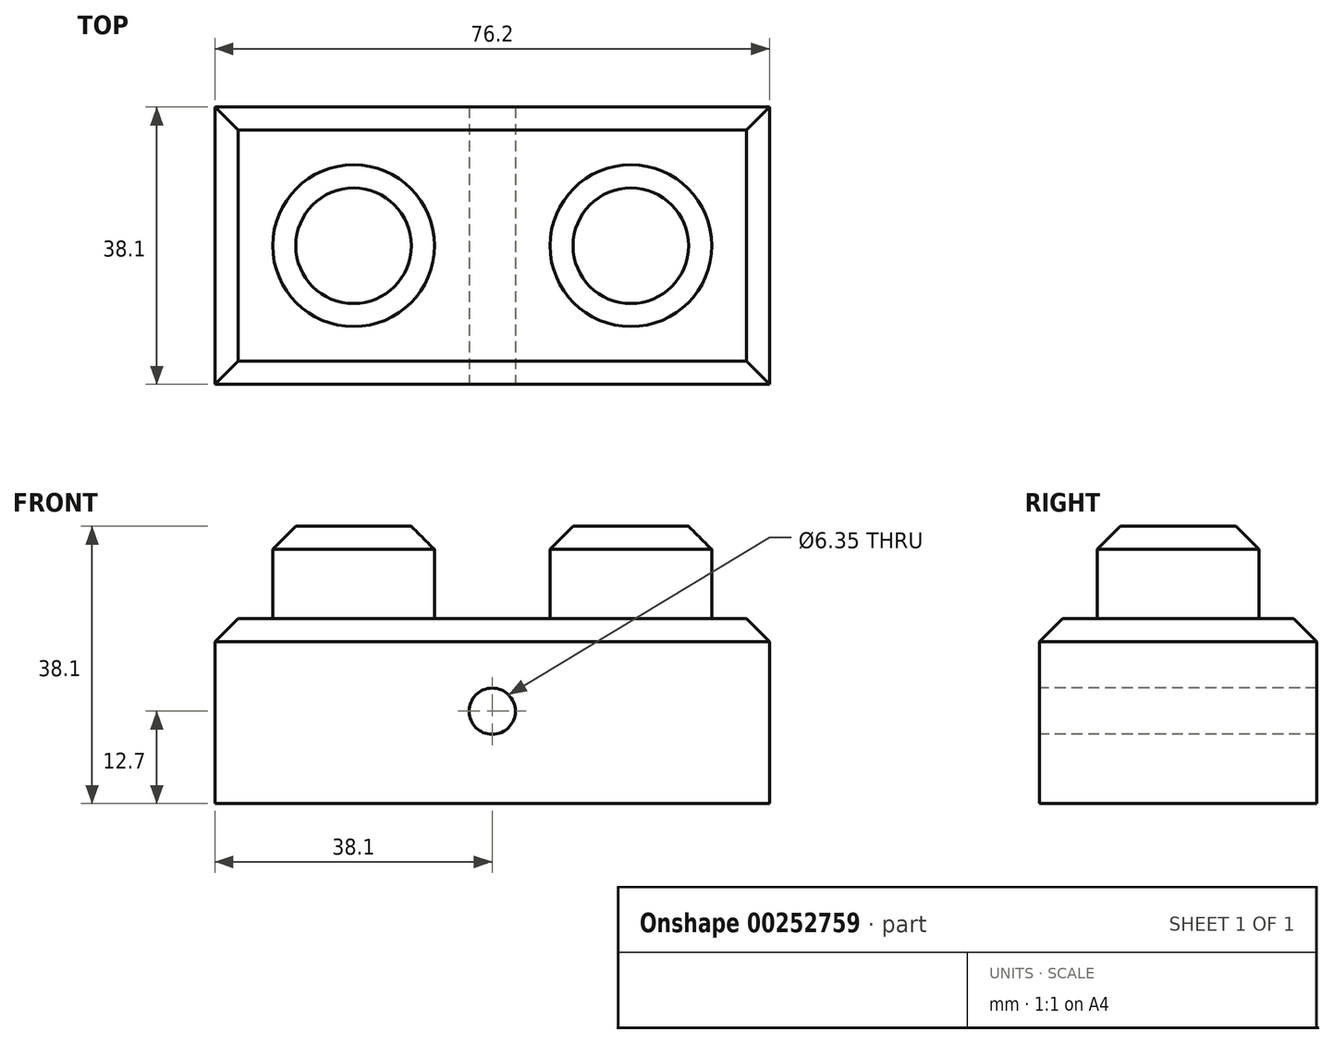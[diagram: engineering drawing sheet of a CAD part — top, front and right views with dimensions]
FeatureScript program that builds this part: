
annotation { "Feature Type Name" : "Feature", "Feature Type Description" : "" }
export const myFeature = defineFeature(function(context is Context, id is Id, definition is map)
    precondition{}
    {
        {
            var Q0;
            Q0=qCreatedBy(makeId("Top.planeOp"),FACE);
            var sketch = newSketch(context, id + "F0", { "sketchPlane" : qUnion([Q0])});
            skLineSegment(sketch, "E0.bottom", {"start": v(0, 0) * mm, "end": v(76.2, 0) * mm});
            skLineSegment(sketch, "E0.top", {"start": v(0, -38.1) * mm, "end": v(76.2, -38.1) * mm});
            skLineSegment(sketch, "E0.left", {"start": v(0, 0) * mm, "end": v(0, -38.1) * mm});
            skLineSegment(sketch, "E0.right", {"start": v(76.2, 0) * mm, "end": v(76.2, -38.1) * mm});
            skSolve(sketch);
        }
        {
            var Q0;
            Q0 = qSketchRegion(id + "F0", true);
            extrude(context, id + "F1", {"entities" : qUnion([Q0]), "depth" : 25.4 * mm});
        }
        {
            var Q0;
            Q0=makeQuery(id+"F1.opExtrude","CAP_FACE",FACE,{"disambiguationData":[OSD([sQuery(id+"F0.wireOp",EDGE,"E0.bottom"),sQuery(id+"F0.wireOp",EDGE,"E0.top"),sQuery(id+"F0.wireOp",EDGE,"E0.left"),sQuery(id+"F0.wireOp",EDGE,"E0.right")])],"isStart":false});
            var sketch = newSketch(context, id + "F2", { "sketchPlane" : qUnion([Q0])});
            skCircle(sketch, "E1", {"center": v(19.05, -19.05) * mm, "radius": 11.11 * mm});
            skCircle(sketch, "E2", {"center": v(57.15, -19.05) * mm, "radius": 11.11 * mm});
            skSolve(sketch);
        }
        {
            var Q0;
            Q0 = qSketchRegion(id + "F2", true);
            extrude(context, id + "F3", {"entities" : qUnion([Q0]), "operationType" : NewBodyOperationType.ADD, "depth" : 12.7 * mm});
        }
        {
            var Q0;
            Q0=makeQuery(id+"F1.opExtrude","SWEPT_FACE",FACE,{"disambiguationData":[OSD([sQuery(id+"F0.wireOp",EDGE,"E0.top")])]});
            var sketch = newSketch(context, id + "F4", { "sketchPlane" : qUnion([Q0])});
            skCircle(sketch, "E3", {"center": v(38.1, 12.7) * mm, "radius": 3.18 * mm});
            skSolve(sketch);
        }
        {
            var Q0;
            Q0 = qSketchRegion(id + "F4", true);
            extrude(context, id + "F5", {"entities" : qUnion([Q0]), "operationType" : NewBodyOperationType.REMOVE, "endBound" : BoundingType.THROUGH_ALL, "oppositeDirection" : true, "depth" : 25.4 * mm, "hasSecondDirection" : true, "secondDirectionBound" : SecondDirectionBoundingType.THROUGH_ALL, "secondDirectionOppositeDirection" : false, "secondDirectionDepth" : 25.4 * mm});
        }
        {
            var Q0;
            Q0=makeQuery(id+"F3.opExtrude","CAP_EDGE",EDGE,{"disambiguationData":[OSD([sQuery(id+"F2.wireOp",EDGE,"E2")])],"isStart":false});
            var Q1;
            Q1=makeQuery(id+"F3.opExtrude","CAP_EDGE",EDGE,{"disambiguationData":[OSD([sQuery(id+"F2.wireOp",EDGE,"E1")])],"isStart":false});
            var Q2;
            Q2=makeQuery(id+"F1.opExtrude","CAP_EDGE",EDGE,{"disambiguationData":[OSD([sQuery(id+"F0.wireOp",EDGE,"E0.top")])],"isStart":false});
            var Q3;
            Q3=makeQuery(id+"F1.opExtrude","CAP_EDGE",EDGE,{"disambiguationData":[OSD([sQuery(id+"F0.wireOp",EDGE,"E0.right")])],"isStart":false});
            var Q4;
            Q4=makeQuery(id+"F1.opExtrude","CAP_EDGE",EDGE,{"disambiguationData":[OSD([sQuery(id+"F0.wireOp",EDGE,"E0.bottom")])],"isStart":false});
            var Q5;
            Q5=makeQuery(id+"F1.opExtrude","CAP_EDGE",EDGE,{"disambiguationData":[OSD([sQuery(id+"F0.wireOp",EDGE,"E0.left")])],"isStart":false});
            chamfer(context, id + "F6", {"entities" : qUnion([Q0, Q1, Q2, Q3, Q4, Q5]), "width" : 3.17 * mm, "tangentPropagation" : true});
        }
    });
